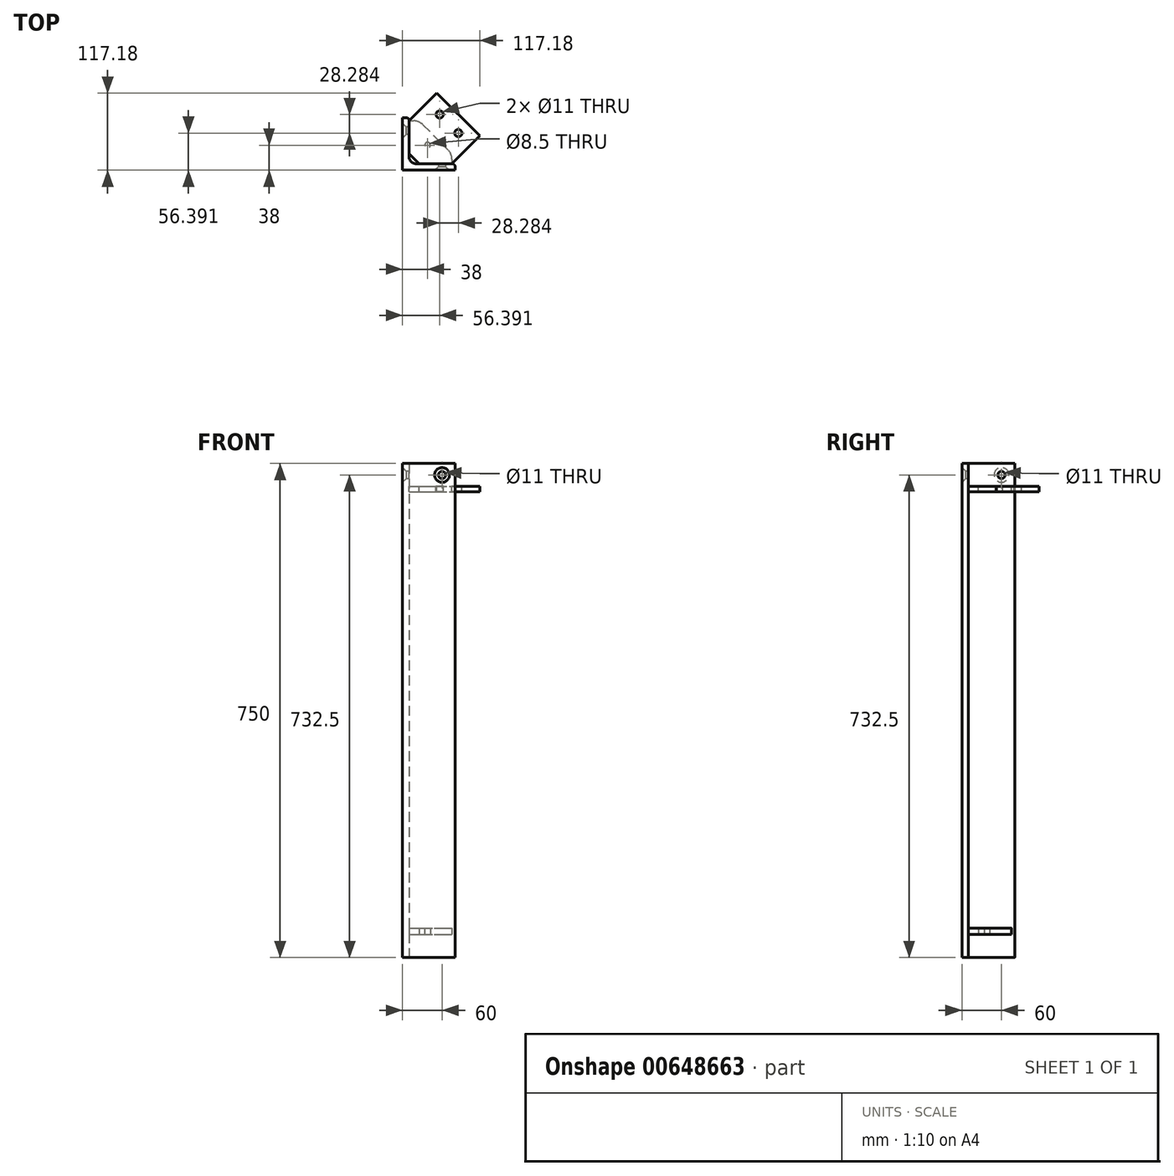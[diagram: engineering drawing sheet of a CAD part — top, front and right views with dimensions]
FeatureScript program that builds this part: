
annotation { "Feature Type Name" : "Feature", "Feature Type Description" : "" }
export const myFeature = defineFeature(function(context is Context, id is Id, definition is map)
    precondition{}
    {
        {
            assignVariable(context, id + "F0", {"variableType" : VariableType.LENGTH, "name" : "t_adapter_unten", "lengthValue" : 10 * mm});
        }
        {
            assignVariable(context, id + "F1", {"variableType" : VariableType.LENGTH, "name" : "t_adapter_oben", "lengthValue" : 8 * mm});
        }
        {
            assignVariable(context, id + "F2", {"variableType" : VariableType.LENGTH, "name" : "l_Tischbein", "lengthValue" : 750 * mm});
        }
        {
            var Q0;
            Q0=qCreatedBy(makeId("Top.planeOp"),FACE);
            var sketch = newSketch(context, id + "F3", { "sketchPlane" : qUnion([Q0])});
            skLineSegment(sketch, "E0.bottom", {"start": v(0, 80) * mm, "end": v(5, 80) * mm});
            skLineSegment(sketch, "E0.top", {"start": v(0, 0) * mm, "end": v(80, 0) * mm});
            skLineSegment(sketch, "E0.left", {"start": v(0, 80) * mm, "end": v(0, 0) * mm});
            skLineSegment(sketch, "E0.right", {"start": v(80, 5) * mm, "end": v(80, 0) * mm});
            skLineSegment(sketch, "E1.top", {"start": v(20, 10) * mm, "end": v(75, 10) * mm});
            skLineSegment(sketch, "E1.left", {"start": v(10, 75) * mm, "end": v(10, 20) * mm});
            skPoint(sketch, "E2.visualSharp", {"position": v(10, 10) * mm});
            skArc(sketch, "E2.filletArc", {"start": v(10, 20) * mm, "mid": v(12.93, 12.93) * mm, "end": v(20, 10) * mm});
            skPoint(sketch, "E3.visualSharp", {"position": v(10, 80) * mm});
            skArc(sketch, "E3.filletArc", {"start": v(10, 75) * mm, "mid": v(8.54, 78.54) * mm, "end": v(5, 80) * mm});
            skPoint(sketch, "E4.visualSharp", {"position": v(80, 10) * mm});
            skArc(sketch, "E4.filletArc", {"start": v(80, 5) * mm, "mid": v(78.54, 8.54) * mm, "end": v(75, 10) * mm});
            skSolve(sketch);
        }
        {
            var Q0;
            Q0=makeQuery(id+"F3.imprint","IMPRINT",FACE,{"disambiguationData":[TD([[makeQuery(id+"F3.imprint","IMPRINT",EDGE,{"derivedFrom":sQuery(id+"F3.wireOp",EDGE,"E0.bottom")}),-1.0]])]});
            extrude(context, id + "F4", {"entities" : qUnion([Q0]), "depth" : getVariable(context, 'l_Tischbein'), "offsetDistance" : 25 * mm});
        }
        {
            var Q0;
            Q0=makeQuery(id+"F4.opExtrude","SWEPT_FACE",FACE,{"disambiguationData":[OSD([sQuery(id+"F3.wireOp",EDGE,"E0.top")])]});
            var sketch = newSketch(context, id + "F5", { "sketchPlane" : qUnion([Q0])});
            skPoint(sketch, "E5", {"position": v(60, 732.5) * mm});
            skSolve(sketch);
        }
        {
            var Q0;
            Q0=sQuery(id+"F5.wireOp",VERTEX,"E5");
            var Q1;
            Q1=makeQuery(id+"F4.opExtrude","SWEPT_BODY",BODY,{"disambiguationData":[OSD([sQuery(id+"F3.wireOp",EDGE,"E0.bottom"),sQuery(id+"F3.wireOp",EDGE,"E0.top"),sQuery(id+"F3.wireOp",EDGE,"E0.left"),sQuery(id+"F3.wireOp",EDGE,"E0.right"),sQuery(id+"F3.wireOp",EDGE,"E1.top"),sQuery(id+"F3.wireOp",EDGE,"E1.left"),sQuery(id+"F3.wireOp",EDGE,"E2.filletArc"),sQuery(id+"F3.wireOp",EDGE,"E3.filletArc"),sQuery(id+"F3.wireOp",EDGE,"E4.filletArc")])]});
            hole(context, id + "F6", {"style" : HoleStyle.C_SINK, "endStyle" : HoleEndStyle.THROUGH, "standardTappedOrClearance" : lookupTablePath({ "fit" : "Normal", "standard" : "ISO", "size" : "M10", "type" : "Clearance" }), "standardBlindInLast" : lookupTablePath({ "fit" : "Normal", "standard" : "ISO", "engagement" : "75%", "pitch" : "1.5 mm", "size" : "M10", "type" : "Clearance & tapped" }), "holeDiameter" : 11 * mm, "cSinkDiameter" : 22.4 * mm, "cSinkAngle" : 90 * degree, "majorDiameter" : 5 * mm, "isTappedThrough" : true, "tappedDepth" : 12 * mm, "tapClearance" : 3, "locations" : qUnion([Q0]), "scope" : qUnion([Q1])});
        }
        {
            var Q0;
            Q0=makeQuery(id+"F4.opExtrude","SWEPT_FACE",FACE,{"disambiguationData":[OSD([sQuery(id+"F3.wireOp",EDGE,"E0.left")])]});
            var sketch = newSketch(context, id + "F7", { "sketchPlane" : qUnion([Q0])});
            skPoint(sketch, "E6", {"position": v(-60, 732.5) * mm});
            skSolve(sketch);
        }
        {
            var Q0;
            Q0=sQuery(id+"F7.wireOp",VERTEX,"E6");
            var Q1;
            Q1=makeQuery(id+"F4.opExtrude","SWEPT_BODY",BODY,{"disambiguationData":[OSD([sQuery(id+"F3.wireOp",EDGE,"E0.bottom"),sQuery(id+"F3.wireOp",EDGE,"E0.top"),sQuery(id+"F3.wireOp",EDGE,"E0.left"),sQuery(id+"F3.wireOp",EDGE,"E0.right"),sQuery(id+"F3.wireOp",EDGE,"E1.top"),sQuery(id+"F3.wireOp",EDGE,"E1.left"),sQuery(id+"F3.wireOp",EDGE,"E2.filletArc"),sQuery(id+"F3.wireOp",EDGE,"E3.filletArc"),sQuery(id+"F3.wireOp",EDGE,"E4.filletArc")])]});
            hole(context, id + "F8", {"style" : HoleStyle.C_SINK, "endStyle" : HoleEndStyle.THROUGH, "standardTappedOrClearance" : lookupTablePath({ "fit" : "Normal", "standard" : "ISO", "size" : "M10", "type" : "Clearance" }), "standardBlindInLast" : lookupTablePath({ "fit" : "Normal", "standard" : "ISO", "engagement" : "75%", "pitch" : "1.5 mm", "size" : "M10", "type" : "Clearance & tapped" }), "holeDiameter" : 11 * mm, "cSinkDiameter" : 22.4 * mm, "cSinkAngle" : 90 * degree, "majorDiameter" : 5 * mm, "isTappedThrough" : true, "tappedDepth" : 12 * mm, "tapClearance" : 3, "locations" : qUnion([Q0]), "scope" : qUnion([Q1])});
        }
        {
            var Q0;
            Q0=makeQuery(id+"F4.opExtrude","CAP_FACE",FACE,{"disambiguationData":[OSD([sQuery(id+"F3.wireOp",EDGE,"E0.bottom"),sQuery(id+"F3.wireOp",EDGE,"E0.top"),sQuery(id+"F3.wireOp",EDGE,"E0.left"),sQuery(id+"F3.wireOp",EDGE,"E0.right"),sQuery(id+"F3.wireOp",EDGE,"E1.top"),sQuery(id+"F3.wireOp",EDGE,"E1.left"),sQuery(id+"F3.wireOp",EDGE,"E2.filletArc"),sQuery(id+"F3.wireOp",EDGE,"E3.filletArc"),sQuery(id+"F3.wireOp",EDGE,"E4.filletArc")])],"isStart":false});
            cPlane(context, id + "F9", {"entities" : qUnion([Q0]), "cplaneType" : CPlaneType.OFFSET, "offset" : 35 * mm, "oppositeDirection" : true, "width" : 150 * mm, "height" : 150 * mm});
        }
        {
            var Q0;
            Q0=makeQuery(id+"F4.opExtrude","CAP_FACE",FACE,{"disambiguationData":[OSD([sQuery(id+"F3.wireOp",EDGE,"E0.bottom"),sQuery(id+"F3.wireOp",EDGE,"E0.top"),sQuery(id+"F3.wireOp",EDGE,"E0.left"),sQuery(id+"F3.wireOp",EDGE,"E0.right"),sQuery(id+"F3.wireOp",EDGE,"E1.top"),sQuery(id+"F3.wireOp",EDGE,"E1.left"),sQuery(id+"F3.wireOp",EDGE,"E2.filletArc"),sQuery(id+"F3.wireOp",EDGE,"E3.filletArc"),sQuery(id+"F3.wireOp",EDGE,"E4.filletArc")])],"isStart":true});
            cPlane(context, id + "F10", {"entities" : qUnion([Q0]), "cplaneType" : CPlaneType.OFFSET, "offset" : 35 * mm, "oppositeDirection" : true, "width" : 150 * mm, "height" : 150 * mm});
        }
        {
            var Q0;
            Q0=qCreatedBy(id+"F9.planeOp",FACE);
            var sketch = newSketch(context, id + "F11", { "sketchPlane" : qUnion([Q0])});
            skLineSegment(sketch, "E7.0", {"start": v(10, 75) * mm, "end": v(10, 25) * mm});
            skLineSegment(sketch, "E7.1", {"start": v(25, 10) * mm, "end": v(75, 10) * mm});
            skLineSegment(sketch, "E8", {"start": v(0, 0) * mm, "end": v(84.68, 84.68) * mm, "construction": true});
            skLineSegment(sketch, "E9", {"start": v(75, 10) * mm, "end": v(25, 10) * mm});
            skLineSegment(sketch, "E10", {"start": v(10, 25) * mm, "end": v(25, 10) * mm});
            skLineSegment(sketch, "E11", {"start": v(10, 75) * mm, "end": v(52.18, 117.18) * mm});
            skLineSegment(sketch, "E12", {"start": v(52.18, 117.18) * mm, "end": v(117.18, 52.18) * mm});
            skLineSegment(sketch, "E13", {"start": v(117.18, 52.18) * mm, "end": v(75, 10) * mm});
            skPoint(sketch, "E14", {"position": v(56.4, 84.68) * mm});
            skPoint(sketch, "E15", {"position": v(84.68, 56.4) * mm});
            skLineSegment(sketch, "E16", {"start": v(38.03, 103.03) * mm, "end": v(103.03, 38.03) * mm, "construction": true});
            skSolve(sketch);
        }
        {
            var Q0;
            Q0=makeQuery(id+"F11.imprint","IMPRINT",FACE,{"disambiguationData":[TD([[makeQuery(id+"F11.imprint","IMPRINT",EDGE,{"derivedFrom":sQuery(id+"F11.wireOp",EDGE,"E7.0")}),1.0]])]});
            extrude(context, id + "F12", {"entities" : qUnion([Q0]), "oppositeDirection" : true, "depth" : getVariable(context, 't_adapter_oben'), "offsetDistance" : 25 * mm});
        }
        {
            var Q0;
            Q0=qCreatedBy(id+"F10.planeOp",FACE);
            var sketch = newSketch(context, id + "F13", { "sketchPlane" : qUnion([Q0])});
            skLineSegment(sketch, "E17.0", {"start": v(10, -75) * mm, "end": v(10, -25) * mm});
            skLineSegment(sketch, "E17.1", {"start": v(25, -10) * mm, "end": v(75, -10) * mm});
            skLineSegment(sketch, "E17.2", {"start": v(10, -75) * mm, "end": v(10, -25) * mm});
            skLineSegment(sketch, "E17.3", {"start": v(0, 0) * mm, "end": v(84.68, -84.68) * mm});
            skLineSegment(sketch, "E17.4", {"start": v(75, -10) * mm, "end": v(25, -10) * mm});
            skLineSegment(sketch, "E17.6", {"start": v(10, -25) * mm, "end": v(25, -10) * mm});
            skLineSegment(sketch, "E18", {"start": v(10, -75) * mm, "end": v(25, -75) * mm});
            skLineSegment(sketch, "E19", {"start": v(25, -75) * mm, "end": v(75, -25) * mm});
            skLineSegment(sketch, "E20", {"start": v(75, -25) * mm, "end": v(75, -10) * mm});
            skPoint(sketch, "E21", {"position": v(38, -38) * mm});
            skSolve(sketch);
        }
        {
            var Q0;
            Q0 = qSketchRegion(id + "F13", true);
            extrude(context, id + "F14", {"entities" : qUnion([Q0]), "oppositeDirection" : true, "depth" : getVariable(context, 't_adapter_unten'), "offsetDistance" : 25 * mm});
        }
        {
            var Q0;
            Q0=makeQuery(id+"F14.opExtrude","SWEPT_EDGE",EDGE,{"disambiguationData":[OSD([sQuery(id+"F13.wireOp",EDGE,"E18"),sQuery(id+"F13.wireOp",EDGE,"E19")])]});
            var Q1;
            Q1=makeQuery(id+"F14.opExtrude","SWEPT_EDGE",EDGE,{"disambiguationData":[OSD([sQuery(id+"F13.wireOp",EDGE,"E19"),sQuery(id+"F13.wireOp",EDGE,"E20")])]});
            fillet(context, id + "F15", {"entities" : qUnion([Q0, Q1]), "radius" : 20 * mm, "tangentPropagation" : true, "allowEdgeOverflow" : false});
        }
        {
            var Q0;
            Q0=sQuery(id+"F13.wireOp",VERTEX,"E21");
            var Q1;
            Q1=makeQuery(id+"F14.opExtrude","SWEPT_BODY",BODY,{"disambiguationData":[OSD([sQuery(id+"F13.wireOp",EDGE,"E17.2"),sQuery(id+"F13.wireOp",EDGE,"E17.4"),sQuery(id+"F13.wireOp",EDGE,"E17.6"),sQuery(id+"F13.wireOp",EDGE,"E18"),sQuery(id+"F13.wireOp",EDGE,"E19"),sQuery(id+"F13.wireOp",EDGE,"E20")])]});
            hole(context, id + "F16", {"style" : HoleStyle.SIMPLE, "endStyle" : HoleEndStyle.THROUGH, "standardTappedOrClearance" : lookupTablePath({ "standard" : "ISO", "engagement" : "75%", "pitch" : "1.5 mm", "size" : "M10", "type" : "Tapped" }), "standardBlindInLast" : lookupTablePath({ "standard" : "ISO", "fit" : "Normal", "engagement" : "75%", "pitch" : "1.5 mm", "size" : "M10", "type" : "Clearance & tapped" }), "holeDiameter" : 8.5 * mm, "majorDiameter" : 10 * mm, "showTappedDepth" : true, "tappedDepth" : 12 * mm, "tapClearance" : 3, "locations" : qUnion([Q0]), "scope" : qUnion([Q1])});
        }
        {
            var Q0;
            Q0=sQuery(id+"F11.wireOp",VERTEX,"E14");
            var Q1;
            Q1=sQuery(id+"F11.wireOp",VERTEX,"E15");
            var Q2;
            Q2=makeQuery(id+"F12.opExtrude","SWEPT_BODY",BODY,{"disambiguationData":[OSD([sQuery(id+"F11.wireOp",EDGE,"E7.0"),sQuery(id+"F11.wireOp",EDGE,"E9"),sQuery(id+"F11.wireOp",EDGE,"E10"),sQuery(id+"F11.wireOp",EDGE,"E11"),sQuery(id+"F11.wireOp",EDGE,"E12"),sQuery(id+"F11.wireOp",EDGE,"E13")])]});
            hole(context, id + "F17", {"style" : HoleStyle.SIMPLE, "endStyle" : HoleEndStyle.THROUGH, "holeDiameter" : 11 * mm, "majorDiameter" : 5 * mm, "isTappedThrough" : true, "tappedDepth" : 12 * mm, "tapClearance" : 3, "locations" : qUnion([Q0, Q1]), "scope" : qUnion([Q2])});
        }
    });
